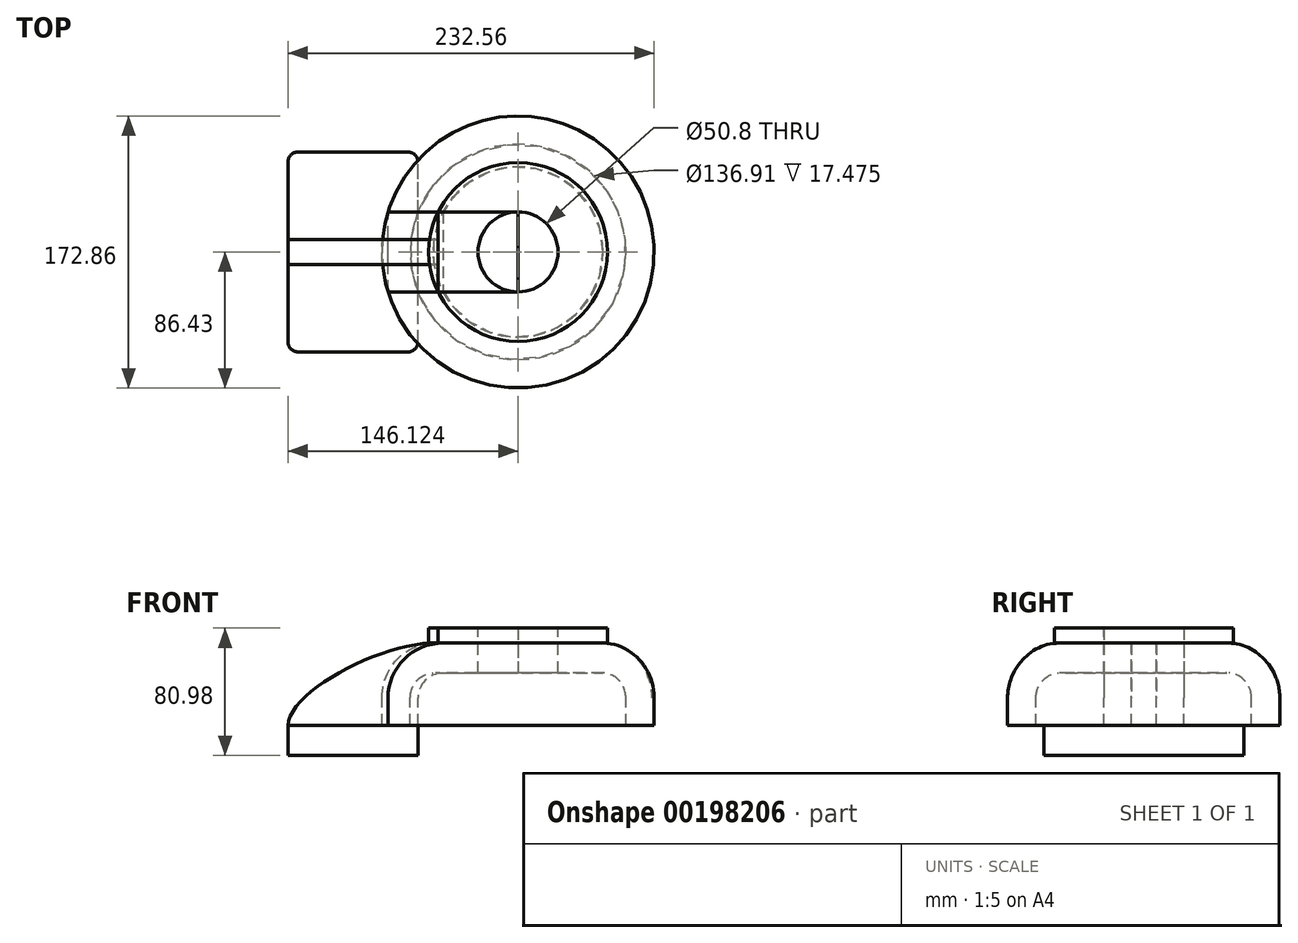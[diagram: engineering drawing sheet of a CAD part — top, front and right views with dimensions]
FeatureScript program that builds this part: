
annotation { "Feature Type Name" : "Feature", "Feature Type Description" : "" }
export const myFeature = defineFeature(function(context is Context, id is Id, definition is map)
    precondition{}
    {
        {
            var Q0;
            Q0=qCreatedBy(makeId("Front.planeOp"),FACE);
            var sketch = newSketch(context, id + "F0", { "sketchPlane" : qUnion([Q0])});
            skLineSegment(sketch, "E0.bottom", {"start": v(-41.27, -9.53) * mm, "end": v(41.28, -9.53) * mm});
            skLineSegment(sketch, "E0.top", {"start": v(-41.28, 9.53) * mm, "end": v(41.28, 9.53) * mm});
            skLineSegment(sketch, "E0.left", {"start": v(-41.28, -9.53) * mm, "end": v(-41.28, 9.53) * mm});
            skLineSegment(sketch, "E0.right", {"start": v(41.28, -9.53) * mm, "end": v(41.28, 9.52) * mm});
            skPoint(sketch, "E0.middle", {"position": v(0, 0) * mm});
            skLineSegment(sketch, "E1.bottom", {"start": v(54.04, 71.45) * mm, "end": v(104.84, 71.45) * mm});
            skLineSegment(sketch, "E1.top", {"start": v(54.04, 42.88) * mm, "end": v(104.84, 42.88) * mm});
            skLineSegment(sketch, "E1.left", {"start": v(54.04, 71.45) * mm, "end": v(54.04, 42.88) * mm});
            skLineSegment(sketch, "E1.right", {"start": v(104.84, 71.45) * mm, "end": v(104.84, 42.88) * mm});
            skPoint(sketch, "E1.middle", {"position": v(79.44, 57.16) * mm});
            skLineSegment(sketch, "E2", {"start": v(41.28, 9.52) * mm, "end": v(41.28, 27) * mm});
            skArc(sketch, "E3", {"start": v(41.27, 27) * mm, "mid": v(45.92, 38.23) * mm, "end": v(57.15, 42.88) * mm});
            skLineSegment(sketch, "E4", {"start": v(57.15, 42.88) * mm, "end": v(78.27, 42.88) * mm});
            skLineSegment(sketch, "E5.0", {"start": v(57.15, 61.93) * mm, "end": v(78.27, 61.93) * mm});
            skArc(sketch, "E5.1", {"start": v(22.22, 27) * mm, "mid": v(32.45, 51.7) * mm, "end": v(57.15, 61.93) * mm});
            skLineSegment(sketch, "E5.2", {"start": v(22.22, 9.52) * mm, "end": v(22.22, 27) * mm});
            skFitSpline(sketch, "E6", {"points": [v(-41.27, 9.52) * mm, v(57.15, 61.93) * mm], "startDerivative": vector(1.93, 69.05) * mm, "endDerivative": vector(102.23, -8.79) * mm});
            skSolve(sketch);
        }
        {
            var Q0;
            Q0=makeQuery(id+"F0.imprint","IMPRINT",FACE,{"disambiguationData":[TD([[makeQuery(id+"F0.imprint","IMPRINT",EDGE,{"derivedFrom":sQuery(id+"F0.wireOp",EDGE,"E0.bottom")}),1.0]])]});
            extrude(context, id + "F1", {"entities" : qUnion([Q0]), "endBound" : BoundingType.SYMMETRIC, "depth" : 127 * mm});
        }
        {
            var Q0;
            {var subQ0=sQuery(id+"F0.wireOp",EDGE,"E2");Q0=makeQuery(id+"F0.imprint","IMPRINT",FACE,{"disambiguationData":[TD([[makeQuery(id+"F0.imprint","IMPRINT",EDGE,{"derivedFrom":subQ0}),1.0]])]});}
            var Q1;
            {var subQ1=sQuery(id+"F0.wireOp",EDGE,"E1.bottom");Q1=makeQuery(id+"F0.imprint","IMPRINT",FACE,{"disambiguationData":[TD([[makeQuery(id+"F0.imprint","IMPRINT",EDGE,{"derivedFrom":subQ1}),-1.0]])]});}
            extrude(context, id + "F2", {"entities" : qUnion([Q0, Q1]), "operationType" : NewBodyOperationType.ADD, "endBound" : BoundingType.SYMMETRIC, "depth" : 50.8 * mm});
        }
        {
            var Q0;
            {var subQ0=sQuery(id+"F0.wireOp",EDGE,"E5.2");Q0=makeQuery(id+"F0.imprint","IMPRINT",FACE,{"disambiguationData":[TD([[makeQuery(id+"F0.imprint","IMPRINT",EDGE,{"derivedFrom":subQ0}),1.0]])]});}
            extrude(context, id + "F3", {"entities" : qUnion([Q0]), "endBound" : BoundingType.SYMMETRIC, "depth" : 15.88 * mm});
        }
        {
            var Q0;
            Q0=makeQuery(id+"F2.opExtrude","CAP_FACE",FACE,{"disambiguationData":[OSD([sQuery(id+"F0.wireOp",EDGE,"E0.top"),sQuery(id+"F0.wireOp",EDGE,"E1.bottom"),sQuery(id+"F0.wireOp",EDGE,"E1.top"),sQuery(id+"F0.wireOp",EDGE,"E1.left"),sQuery(id+"F0.wireOp",EDGE,"E1.right"),sQuery(id+"F0.wireOp",EDGE,"E2"),sQuery(id+"F0.wireOp",EDGE,"E3"),sQuery(id+"F0.wireOp",EDGE,"E4"),sQuery(id+"F0.wireOp",EDGE,"E5.1"),sQuery(id+"F0.wireOp",EDGE,"E5.2"),sQuery(id+"F0.wireOp",EDGE,"E6")])],"isStart":true});
            var Q1;
            Q1=sQuery(id+"F0.wireOp",EDGE,"E1.right");
            revolve(context, id + "F4", {"entities" : qUnion([Q0]), "axis" : qUnion([Q1]), "revolveType" : RevolveType.FULL});
        }
        {
            var Q0;
            Q0=makeQuery(id+"F1.opExtrude","CAP_EDGE",EDGE,{"disambiguationData":[OSD([sQuery(id+"F0.wireOp",EDGE,"E0.right")])],"isStart":false});
            var Q1;
            Q1=makeQuery(id+"F1.opExtrude","CAP_EDGE",EDGE,{"disambiguationData":[OSD([sQuery(id+"F0.wireOp",EDGE,"E0.left")])],"isStart":false});
            var Q2;
            Q2=makeQuery(id+"F1.opExtrude","CAP_EDGE",EDGE,{"disambiguationData":[OSD([sQuery(id+"F0.wireOp",EDGE,"E0.right")])],"isStart":true});
            var Q3;
            Q3=makeQuery(id+"F1.opExtrude","CAP_EDGE",EDGE,{"disambiguationData":[OSD([sQuery(id+"F0.wireOp",EDGE,"E0.left")])],"isStart":true});
            fillet(context, id + "F5", {"entities" : qUnion([Q0, Q1, Q2, Q3]), "radius" : 6.35 * mm, "tangentPropagation" : true, "allowEdgeOverflow" : false});
        }
    });
